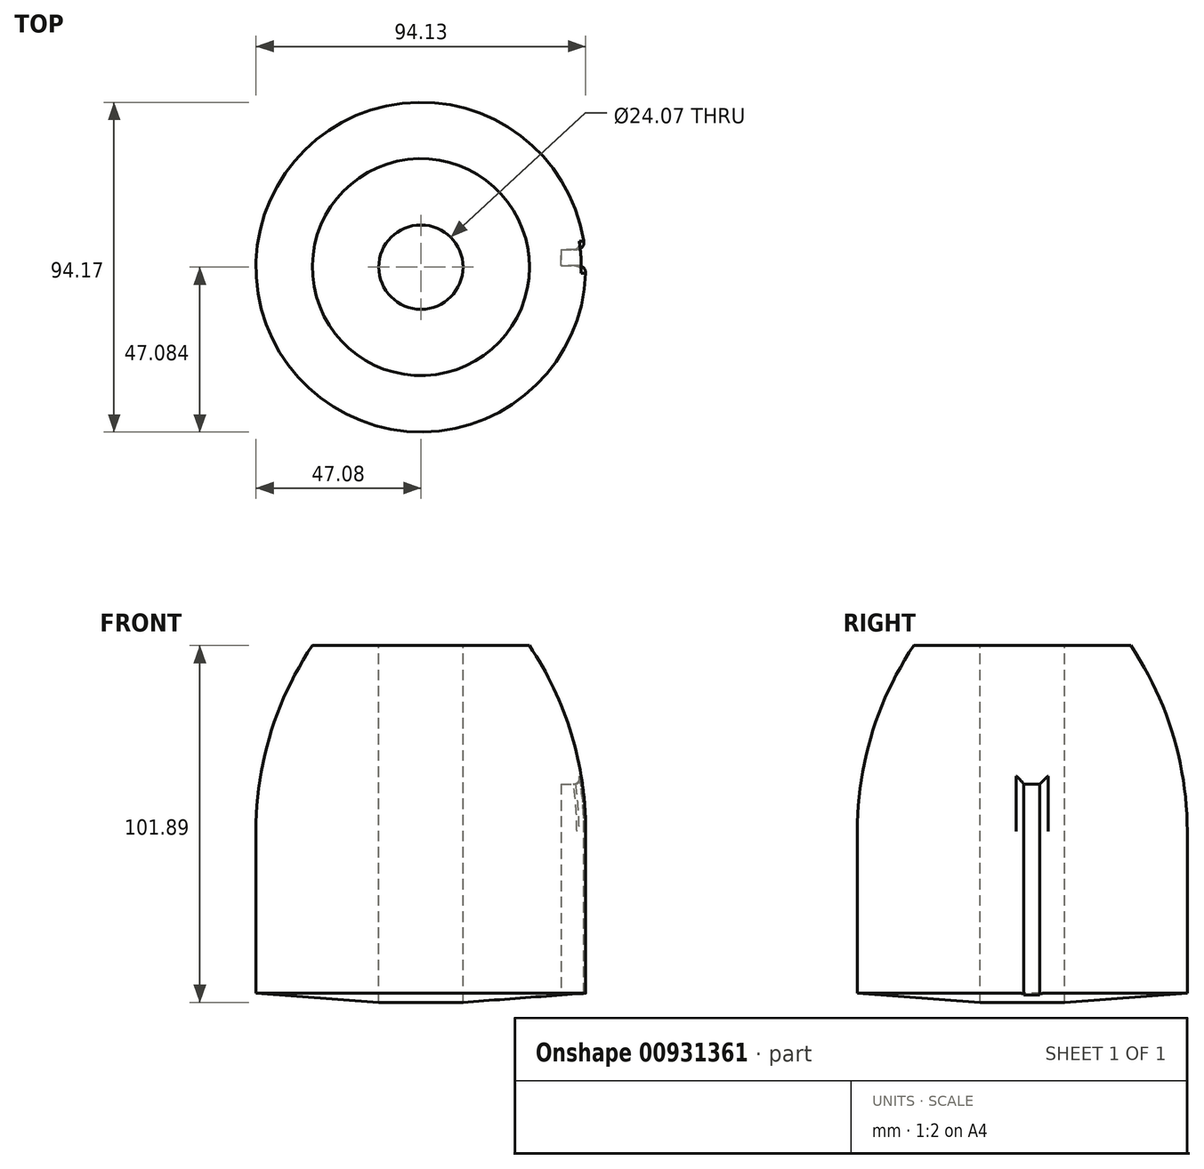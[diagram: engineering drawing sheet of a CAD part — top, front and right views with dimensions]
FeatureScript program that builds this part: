
annotation { "Feature Type Name" : "Feature", "Feature Type Description" : "" }
export const myFeature = defineFeature(function(context is Context, id is Id, definition is map)
    precondition{}
    {
        {
            var Q0;
            Q0=qCreatedBy(makeId("Right.planeOp"),FACE);
            var sketch = newSketch(context, id + "F0", { "sketchPlane" : qUnion([Q0])});
            skLineSegment(sketch, "E0", {"start": v(0, 59.44) * mm, "end": v(0, -42.45) * mm, "construction": true});
            skLineSegment(sketch, "E1", {"start": v(0, 59.44) * mm, "end": v(18.94, 59.44) * mm});
            skLineSegment(sketch, "E2", {"start": v(35.05, 6.44) * mm, "end": v(35.05, -39.85) * mm});
            skLineSegment(sketch, "E3", {"start": v(35.05, -39.85) * mm, "end": v(0, -42.45) * mm});
            skArc(sketch, "E4", {"start": v(35.05, 6.44) * mm, "mid": v(30.93, 34.13) * mm, "end": v(18.94, 59.44) * mm});
            skLineSegment(sketch, "E5", {"start": v(0, 59.44) * mm, "end": v(0, -42.45) * mm});
            skLineSegment(sketch, "E6", {"start": v(-12.04, 70.82) * mm, "end": v(-12.04, -63.91) * mm, "construction": true});
            skSolve(sketch);
        }
        {
            var Q0;
            Q0 = qSketchRegion(id + "F0", true);
            var Q1;
            Q1=sQuery(id+"F0.wireOp",EDGE,"E6");
            revolve(context, id + "F1", {"surfaceOperationType" : NewSurfaceOperationType.NEW, "entities" : qUnion([Q0]), "axis" : qUnion([Q1]), "revolveType" : RevolveType.FULL});
        }
        {
            var Q0;
            Q0=qCreatedBy(makeId("Right.planeOp"),FACE);
            cPlane(context, id + "F2", {"entities" : qUnion([Q0]), "cplaneType" : CPlaneType.OFFSET, "offset" : 50 * mm, "width" : 150 * mm, "height" : 150 * mm});
        }
        {
            var Q0;
            Q0=qCreatedBy(id+"F2.planeOp",FACE);
            var sketch = newSketch(context, id + "F3", { "sketchPlane" : qUnion([Q0])});
            skLineSegment(sketch, "E7.bottom", {"start": v(-11.66, 19.87) * mm, "end": v(-7, 19.87) * mm});
            skLineSegment(sketch, "E7.top", {"start": v(-11.66, -44.53) * mm, "end": v(-7, -44.53) * mm});
            skLineSegment(sketch, "E7.left", {"start": v(-11.66, 19.87) * mm, "end": v(-11.66, -44.53) * mm});
            skLineSegment(sketch, "E7.right", {"start": v(-7, 19.87) * mm, "end": v(-7, -44.53) * mm});
            skSolve(sketch);
        }
        {
            var Q0;
            Q0 = qSketchRegion(id + "F3", true);
            extrude(context, id + "F4", {"entities" : qUnion([Q0]), "operationType" : NewBodyOperationType.REMOVE, "oppositeDirection" : true, "depth" : 10 * mm, "offsetDistance" : 25 * mm});
        }
        {
            var Q0;
            Q0=makeQuery(id+"F4.boolean.opBoolean","INTERSECT",EDGE,{"derivedFrom":[makeQuery(id+"F1.opRevolve","SWEPT_FACE",FACE,{"disambiguationData":[OSD([sQuery(id+"F0.wireOp",EDGE,"E2")])]}),makeQuery(id+"F4.opExtrude","SWEPT_FACE",FACE,{"disambiguationData":[OSD([sQuery(id+"F3.wireOp",EDGE,"E7.right")])]})]});
            var Q1;
            Q1=makeQuery(id+"F4.boolean.opBoolean","INTERSECT",EDGE,{"derivedFrom":[makeQuery(id+"F1.opRevolve","SWEPT_FACE",FACE,{"disambiguationData":[OSD([sQuery(id+"F0.wireOp",EDGE,"E4")])]}),makeQuery(id+"F4.opExtrude","SWEPT_FACE",FACE,{"disambiguationData":[OSD([sQuery(id+"F3.wireOp",EDGE,"E7.right")])]})]});
            var Q2;
            Q2=makeQuery(id+"F4.boolean.opBoolean","INTERSECT",EDGE,{"derivedFrom":[makeQuery(id+"F1.opRevolve","SWEPT_FACE",FACE,{"disambiguationData":[OSD([sQuery(id+"F0.wireOp",EDGE,"E4")])]}),makeQuery(id+"F4.opExtrude","SWEPT_FACE",FACE,{"disambiguationData":[OSD([sQuery(id+"F3.wireOp",EDGE,"E7.left")])]})]});
            var Q3;
            Q3=makeQuery(id+"F4.boolean.opBoolean","INTERSECT",EDGE,{"derivedFrom":[makeQuery(id+"F1.opRevolve","SWEPT_FACE",FACE,{"disambiguationData":[OSD([sQuery(id+"F0.wireOp",EDGE,"E2")])]}),makeQuery(id+"F4.opExtrude","SWEPT_FACE",FACE,{"disambiguationData":[OSD([sQuery(id+"F3.wireOp",EDGE,"E7.left")])]})]});
            var Q4;
            Q4=makeQuery(id+"F4.boolean.opBoolean","INTERSECT",EDGE,{"derivedFrom":[makeQuery(id+"F1.opRevolve","SWEPT_FACE",FACE,{"disambiguationData":[OSD([sQuery(id+"F0.wireOp",EDGE,"E4")])]}),makeQuery(id+"F4.opExtrude","SWEPT_FACE",FACE,{"disambiguationData":[OSD([sQuery(id+"F3.wireOp",EDGE,"E7.bottom")])]})]});
            fillet(context, id + "F5", {"entities" : qUnion([Q0, Q1, Q2, Q3, Q4]), "radius" : 2 * mm, "tangentPropagation" : true, "allowEdgeOverflow" : false});
        }
    });
